# Revit family: Animo Handrail_
name_source: partatom
category: Casework
revit_build: Autodesk Revit Architecture 2012 (Build: 20110916_2132(x64)
units: mm (PartAtom-declared; Revit-internal decimal feet)

## types (20) — shared parameters
Covering Plate = RAL 9010 - White
Manufacturer = Väinö Korpinen Oy
URL = www.korpinen.com
zero-valued in all types: Height

## per-type parameters (varying)
| type | Handrail Color | Keynote | Length | Model |
| 1621 P | RAL 3003 - Red |  | 450 mm  [stored 1.47638 ft] | Animo 1621 P Handrail |
| 1621 | RAL 9010 - White |  | 450 mm  [stored 1.47638 ft] | Animo 1621 Handrail |
| 1621 K | RAL 1004 - Yellow | Handrail | 450 mm  [stored 1.47638 ft] | Animo 1621 K Handrail |
| 1621 H | RAL 7037 - Grey |  | 450 mm  [stored 1.47638 ft] | Animo 1621 H Handrail |
| 1622 | RAL 9010 - White |  | 550 mm | Animo 1622 Handrail |
| 1622 H | RAL 7037 - Grey |  | 550 mm | Animo 1622 K Handrail |
| 1622 K | RAL 1004 - Yellow |  | 550 mm | Animo 1622 K Handrail |
| 1622 P | RAL 3003 - Red |  | 550 mm | Animo 1622 P Handrail |
| 1625 | RAL 9010 - White |  | 700 mm  [stored 2.29659 ft] | Animo 1625 Handrail |
| 1625 H | RAL 7037 - Grey |  | 700 mm  [stored 2.29659 ft] | Animo 1625 H Handrail |
| 1625 K | RAL 1004 - Yellow |  | 700 mm  [stored 2.29659 ft] | Animo 1625 K |
| 1625 P | RAL 3003 - Red |  | 700 mm  [stored 2.29659 ft] | Animo 1625 P Handrail |
| 1626 | RAL 9010 - White |  | 800 mm  [stored 2.62467 ft] | Animo 1626 Handrail |
| 1626 H | RAL 7037 - Grey |  | 800 mm  [stored 2.62467 ft] | Animo 1626 H Handrail |
| 1626 K | RAL 1004 - Yellow |  | 800 mm  [stored 2.62467 ft] | Animo 1626 K Handrail |
| 1626 P | RAL 3003 - Red |  | 800 mm  [stored 2.62467 ft] | Animo 1626 P Handrail |
| 1627 | RAL 9010 - White |  | 1000 mm  [stored 3.28084 ft] | Animo 1627 Handrail |
| 1627 H | RAL 7037 - Grey |  | 1000 mm  [stored 3.28084 ft] | Animo 1627 H Handrail |
| 1627 K | RAL 1004 - Yellow |  | 1000 mm  [stored 3.28084 ft] | Animo 1627 K Handrail |
| 1627 P | RAL 3003 - Red |  | 1000 mm  [stored 3.28084 ft] | Animo 1627 P Handrail |

note: [stored X ft] marks values corroborated as IEEE doubles in the binary element streams (Revit-internal decimal feet)

## geometry (parser evidence)
native form markers: Sweep x5
no freeform markers — native parametric forms only
